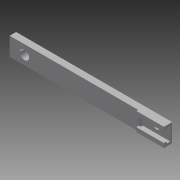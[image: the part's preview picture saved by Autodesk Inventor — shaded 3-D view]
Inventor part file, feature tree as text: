
AUTODESK INVENTOR PART (.ipt)
format: ipt  version: 2013 (Build 170138000, 138)  size: 164,864 bytes
history: native  units: in
note: dims shown in document units (in); Inventor stores cm internally (conversion verified against a paired STEP export)
features: extrude x9, sketch x8
ambient origin geometry x8: Origin, YZ Plane, XZ Plane, XY Plane, X Axis, Y Axis, Z Axis, Center Point
bodies: Solid1 (feature_tree)
feature tree (17):
  extrude  "Extrusion1"  Depth=1.0in
  extrude  "Extrusion2"  Depth=1.5in
  extrude  "Extrusion3"  Depth=0.365in
  extrude  "Extrusion4"  Depth=0.35in TaperAngle=0.0deg
  extrude  "Extrusion5"  Depth=0.1in TaperAngle=0.0deg
  sketch  "Sketch6"  dims[d14=0.2in d15=0.1in d16=0.0in]
  extrude  "Extrusion6"  Depth=0.1in TaperAngle=0.0deg
  extrude  "Extrusion7"  Depth=0.1in TaperAngle=0.0deg
  extrude  "Extrusion8"  Depth=1.5in
  extrude  "Extrusion9"  Depth=0.35in
  sketch  "Sketch1"  dims[d0=8.5in d1=1.0in]
  sketch  "Sketch2"  dims[d2=0.35in d3=0.0in d4=1.5in]
  sketch  "Sketch3"  dims[d5=0.365in d6=0.365in]
  sketch  "Sketch4"  dims[d7=0.35in d8=0.0in d9=0.35in d10=0.0in]
  sketch  "Sketch5"  dims[d11=0.2in d12=0.1in d13=0.0in]
  sketch  "Sketch7"  dims[d19=0.15in d20=0.1in d21=0.0in]
  sketch  "Sketch8"  dims[d22=0.1in d23=0.0in d24=1.5in d25=0.35in d26=0.1in d27=0.0in d28=0.5in d29=1.0in d30=0.0in]
